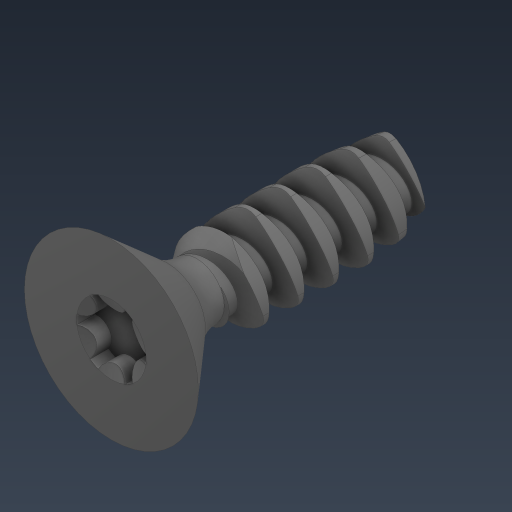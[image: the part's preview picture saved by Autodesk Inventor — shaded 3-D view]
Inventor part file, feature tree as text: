
AUTODESK INVENTOR PART (.ipt)
format: ipt  version: 2024.3 (Build 283343000, 343)  size: 450,560 bytes
history: native  units: in
note: dims shown in document units (in); Inventor stores cm internally (conversion verified against a paired STEP export)
features: revolve x1
ambient origin geometry x8: Origin, YZ Plane, XZ Plane, XY Plane, X Axis, Y Axis, Z Axis, Center Point
bodies: Solid1 (feature_tree)
feature tree (1):
  revolve  "Revolve3"  [1 undecoded]
note: 1 required parameter value undecoded (feature->parameter linkage not recoverable at this tier; creation-order binding heuristic only, values carry confidence <= 0.55)
